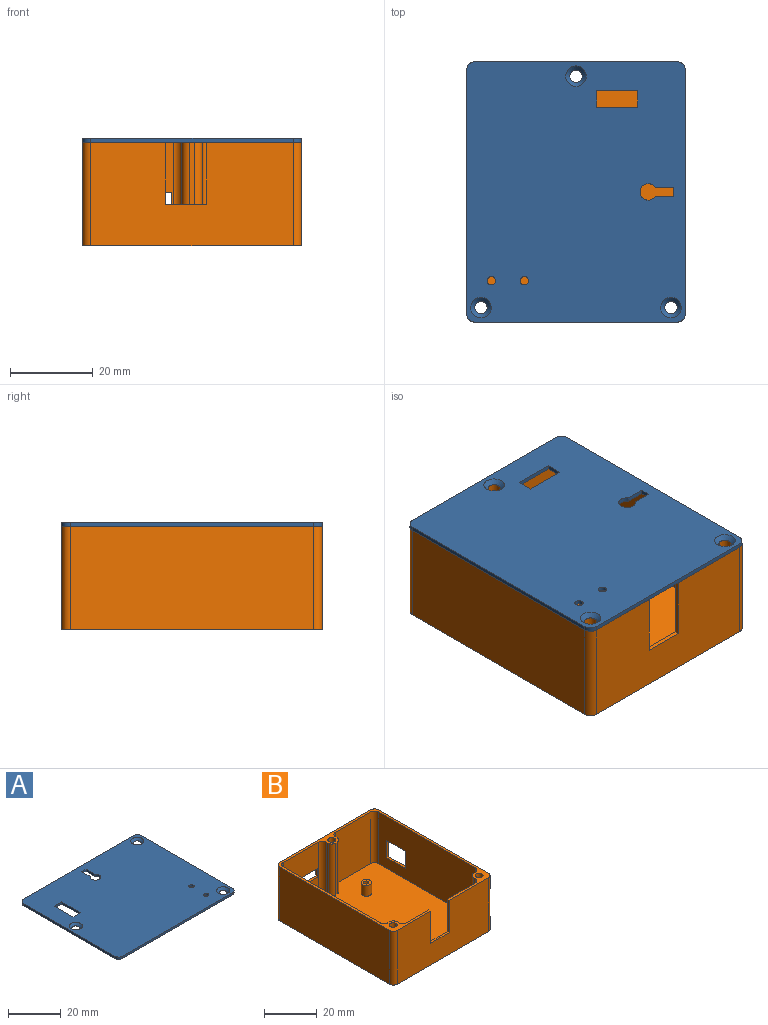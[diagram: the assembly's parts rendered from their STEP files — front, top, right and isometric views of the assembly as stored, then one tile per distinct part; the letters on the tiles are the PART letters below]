
ASSEMBLY  parts=2 mates=1
PART A: 23 faces, bbox 63x53x1 mm
  f0: plane 59x1mm, normal (0,-1,0), area 59mm2, adj f14,f15,f19,f22
  f1: plane 49x1mm, normal (1,0,0), area 49mm2, adj f14,f15,f19,f20
  f2: plane 59x1mm, normal (0,1,0), area 59mm2, adj f14,f15,f20,f21
  f3: plane 4x1mm, normal (0,1,0), area 4mm2, adj f4,f9,f14,f15
  f4: plane 10x1mm, normal (1,0,0), area 10mm2, adj f3,f5,f14,f15
  f5: plane 4x1mm, normal (0,-1,0), area 4mm2, adj f4,f9,f14,f15
  f6: plane 4.52x1mm, normal (-1,0,0), area 4.5mm2, adj f7,f12,f14,f15
  f7: cylinder r=2mm len=4mm, axis (0,0,-1), area 10.1mm2, adj f6,f8,f14,f15
  f8: plane 4.52x1mm, normal (1,0,0), area 4.5mm2, adj f7,f12,f14,f15
  f9: plane 10x1mm, normal (-1,0,0), area 10mm2, adj f3,f5,f14,f15
  f10: cylinder r=1mm len=2mm, axis (0,0,-1), area 6.3mm2, adj f14,f15
  f11: cylinder r=1mm len=2mm, axis (0,0,-1), area 6.3mm2, adj f14,f15
  f12: plane 2.34x1mm, normal (0,-1,0), area 2.3mm2, adj f6,f8,f14,f15
  f13: plane 49x1mm, normal (-1,0,0), area 49mm2, adj f14,f15,f21,f22
  f14: plane 63x53mm, normal (0,0,1), area 3207.8mm2, adj f0,f1,f2,f3,f4,f5,f6,f7
  f15: plane 63x53mm, normal (0,0,-1), area 3245.5mm2, adj f0,f1,f2,f3,f4,f5,f6,f7
  f16: cone r=1.5mm half-angle=45deg, axis (0,0,1), area 17.8mm2, adj f14,f15
  f17: cone r=1.5mm half-angle=45deg, axis (0,0,1), area 17.8mm2, adj f14,f15
  f18: cone r=1.5mm half-angle=45deg, axis (0,0,1), area 17.8mm2, adj f14,f15
  f19: cylinder r=2mm len=2mm, axis (0,0,1), area 3.1mm2, adj f0,f1,f14,f15
  f20: cylinder r=2mm len=2mm, axis (0,0,-1), area 3.1mm2, adj f1,f2,f14,f15
  f21: cylinder r=2mm len=2mm, axis (0,0,1), area 3.1mm2, adj f2,f13,f14,f15
  f22: cylinder r=2mm len=2mm, axis (0,0,-1), area 3.1mm2, adj f0,f13,f14,f15
PART B: 59 faces, bbox 53x63x25 mm
  f0: plane 52x24mm, normal (-1,0,0), area 1168mm2, adj f2,f4,f28,f43,f51,f52,f53,f54
  f1: plane 59x25mm, normal (1,0,0), area 1395mm2, adj f2,f10,f37,f38,f51,f52,f53,f54
  f2: plane 63x53mm, normal (0,0,1), area 271.8mm2, adj f0,f1,f3,f5,f6,f7,f8,f9
  f3: plane 24x19mm, normal (0,-1,0), area 382.1mm2, adj f2,f4,f34,f42,f45,f46,f47
  f4: plane 61x51mm, normal (0,0,1), area 2994.9mm2, adj f0,f3,f5,f6,f11,f12,f13,f14
  f5: plane 37x24mm, normal (0,1,0), area 738mm2, adj f2,f4,f29,f30,f48,f49,f50
  f6: plane 52x24mm, normal (1,0,0), area 1248mm2, adj f2,f4,f31,f42
  f7: plane 59x25mm, normal (-1,0,0), area 1475mm2, adj f2,f10,f36,f39
  f8: plane 49x25mm, normal (0,-1,0), area 1075mm2, adj f2,f10,f36,f37,f48,f49,f50
  f9: plane 49x25mm, normal (0,1,0), area 1151.1mm2, adj f2,f10,f38,f39,f44,f45,f46,f47
  f10: plane 63x53mm, normal (0,0,-1), area 3308.1mm2, adj f1,f7,f8,f9,f19,f20,f21,f22
  f11: plane 24x19mm, normal (0,-1,0), area 456mm2, adj f2,f4,f35,f43
  f12: plane 24x1mm, normal (1,0,0), area 24mm2, adj f2,f4,f32,f35
  f13: plane 24x1mm, normal (-1,0,0), area 24mm2, adj f2,f4,f33,f34
  f14: plane 24x1mm, normal (0,-1,0), area 24mm2, adj f2,f4,f32,f33
  f15: plane 24x1mm, normal (1,0,0), area 24mm2, adj f2,f4,f30,f41
  f16: plane 24x1mm, normal (0,1,0), area 24mm2, adj f2,f4,f31,f41
  f17: plane 24x1mm, normal (-1,0,0), area 24mm2, adj f2,f4,f29,f40
  f18: plane 24x1mm, normal (0,1,0), area 24mm2, adj f2,f4,f28,f40
  f19: cylinder r=1.5mm len=25mm, axis (0,0,1), area 235.6mm2, adj f2,f10
  f20: cylinder r=1.5mm len=25mm, axis (0,0,1), area 235.6mm2, adj f2,f10
  f21: cylinder r=1.5mm len=25mm, axis (0,0,1), area 235.6mm2, adj f2,f10
  f22: cylinder r=1mm len=6mm, axis (0,0,-1), area 37.7mm2, adj f10,f24
  f23: cylinder r=2mm len=5mm, axis (0,0,-1), area 62.8mm2, adj f4,f24
  f24: plane 4x4mm, normal (0,0,1), area 9.4mm2, adj f22,f23
  f25: cylinder r=1mm len=6mm, axis (0,0,-1), area 37.7mm2, adj f10,f27
  f26: cylinder r=2mm len=5mm, axis (0,0,-1), area 62.8mm2, adj f4,f27
  f27: plane 4x4mm, normal (0,0,1), area 9.4mm2, adj f25,f26
  f28: cylinder r=2mm len=24mm, axis (0,0,1), area 75.4mm2, adj f0,f2,f4,f18
  f29: cylinder r=2mm len=24mm, axis (0,0,1), area 75.4mm2, adj f2,f4,f5,f17
  f30: cylinder r=2mm len=24mm, axis (0,0,-1), area 75.4mm2, adj f2,f4,f5,f15
  f31: cylinder r=2mm len=24mm, axis (0,0,1), area 75.4mm2, adj f2,f4,f6,f16
  f32: cylinder r=2mm len=24mm, axis (0,0,1), area 75.4mm2, adj f2,f4,f12,f14
  f33: cylinder r=2mm len=24mm, axis (0,0,-1), area 75.4mm2, adj f2,f4,f13,f14
  f34: cylinder r=2mm len=24mm, axis (0,0,1), area 75.4mm2, adj f2,f3,f4,f13
  f35: cylinder r=2mm len=24mm, axis (0,0,-1), area 75.4mm2, adj f2,f4,f11,f12
  f36: cylinder r=2mm len=25mm, axis (0,0,-1), area 78.5mm2, adj f2,f7,f8,f10
  f37: cylinder r=2mm len=25mm, axis (0,0,1), area 78.5mm2, adj f1,f2,f8,f10
  f38: cylinder r=2mm len=25mm, axis (0,0,-1), area 78.5mm2, adj f1,f2,f9,f10
  f39: cylinder r=2mm len=25mm, axis (0,0,1), area 78.5mm2, adj f2,f7,f9,f10
  f40: cylinder r=2mm len=24mm, axis (0,0,1), area 75.4mm2, adj f2,f4,f17,f18
  f41: cylinder r=2mm len=24mm, axis (0,0,1), area 75.4mm2, adj f2,f4,f15,f16
  f42: cylinder r=2mm len=24mm, axis (0,0,1), area 75.4mm2, adj f2,f3,f4,f6,f44
  f43: cylinder r=2mm len=24mm, axis (0,0,-1), area 75.4mm2, adj f0,f2,f4,f11
  f44: plane 4x1mm, normal (1,0,0), area 4mm2, adj f9,f42,f45,f47
  f45: plane 18.47x1mm, normal (0,0,1), area 18.5mm2, adj f3,f9,f44,f46
  f46: plane 4x1mm, normal (-1,0,0), area 4mm2, adj f3,f9,f45,f47
  f47: plane 18.47x1mm, normal (0,0,-1), area 18.5mm2, adj f3,f9,f44,f46
  f48: plane 15x1mm, normal (-1,0,0), area 15mm2, adj f2,f5,f8,f50
  f49: plane 15x1mm, normal (1,0,0), area 15mm2, adj f2,f5,f8,f50
  f50: plane 10x1mm, normal (0,0,1), area 10mm2, adj f5,f8,f48,f49
  f51: plane 10x1mm, normal (0,0,1), area 10mm2, adj f0,f1,f52,f54
  f52: plane 8x1mm, normal (0,-1,0), area 8mm2, adj f0,f1,f51,f53
  f53: plane 10x1mm, normal (0,0,-1), area 10mm2, adj f0,f1,f52,f54
  f54: plane 8x1mm, normal (0,1,0), area 8mm2, adj f0,f1,f51,f53
  f55: cylinder r=1mm len=5mm, axis (0,0,-1), area 31.4mm2, adj f57,f58
  f56: cylinder r=2mm len=5mm, axis (0,0,-1), area 62.8mm2, adj f4,f57
  f57: plane 4x4mm, normal (0,0,1), area 9.4mm2, adj f55,f56
  f58: plane 2x2mm, normal (0,0,1), area 3.1mm2, adj f55
PLACE A rot(axis=(0,0,-1),90deg) t=(-63.44,9.25,25)mm
PLACE B at identity fixed
MATE slider B.f21 <-> A.f18  axis (0,0,1) through (-36.94,76.95,25)mm
